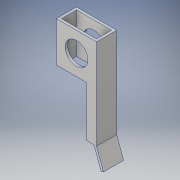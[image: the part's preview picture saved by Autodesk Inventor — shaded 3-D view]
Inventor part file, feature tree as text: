
AUTODESK INVENTOR PART (.ipt)
format: ipt  version: 2016 (Build 200138000, 138)  size: 140,800 bytes
history: native  units: in
note: dims shown in document units (in); Inventor stores cm internally (conversion verified against a paired STEP export)
features: extrude x4, sketch x4
ambient origin geometry x8: Origin, YZ Plane, XZ Plane, XY Plane, X Axis, Y Axis, Z Axis, Center Point
bodies: Solid1 (feature_tree)
feature tree (8):
  extrude  "Extrusion1"  Depth=1.0in
  extrude  "Extrusion2"  Depth=4.5in TaperAngle=0.0deg
  extrude  "Extrusion3"  Depth=2.5in
  extrude  "Extrusion4"  Depth=1.0in
  sketch  "Sketch1"  dims[d0=2.0in d1=1.0in]
  sketch  "Sketch2"  dims[d2=0.125in d3=4.5in d4=0.0in]
  sketch  "Sketch3"  dims[d5=1.5in d6=2.5in]
  sketch  "Sketch4"  dims[d7=1.0in d8=0.0in d9=1.125in d10=1.0in d11=1.0in d12=1.0in d13=0.0in d14=1.0in d15=0.125in d16=0.7559in d17=1.0in d18=0.0in]
